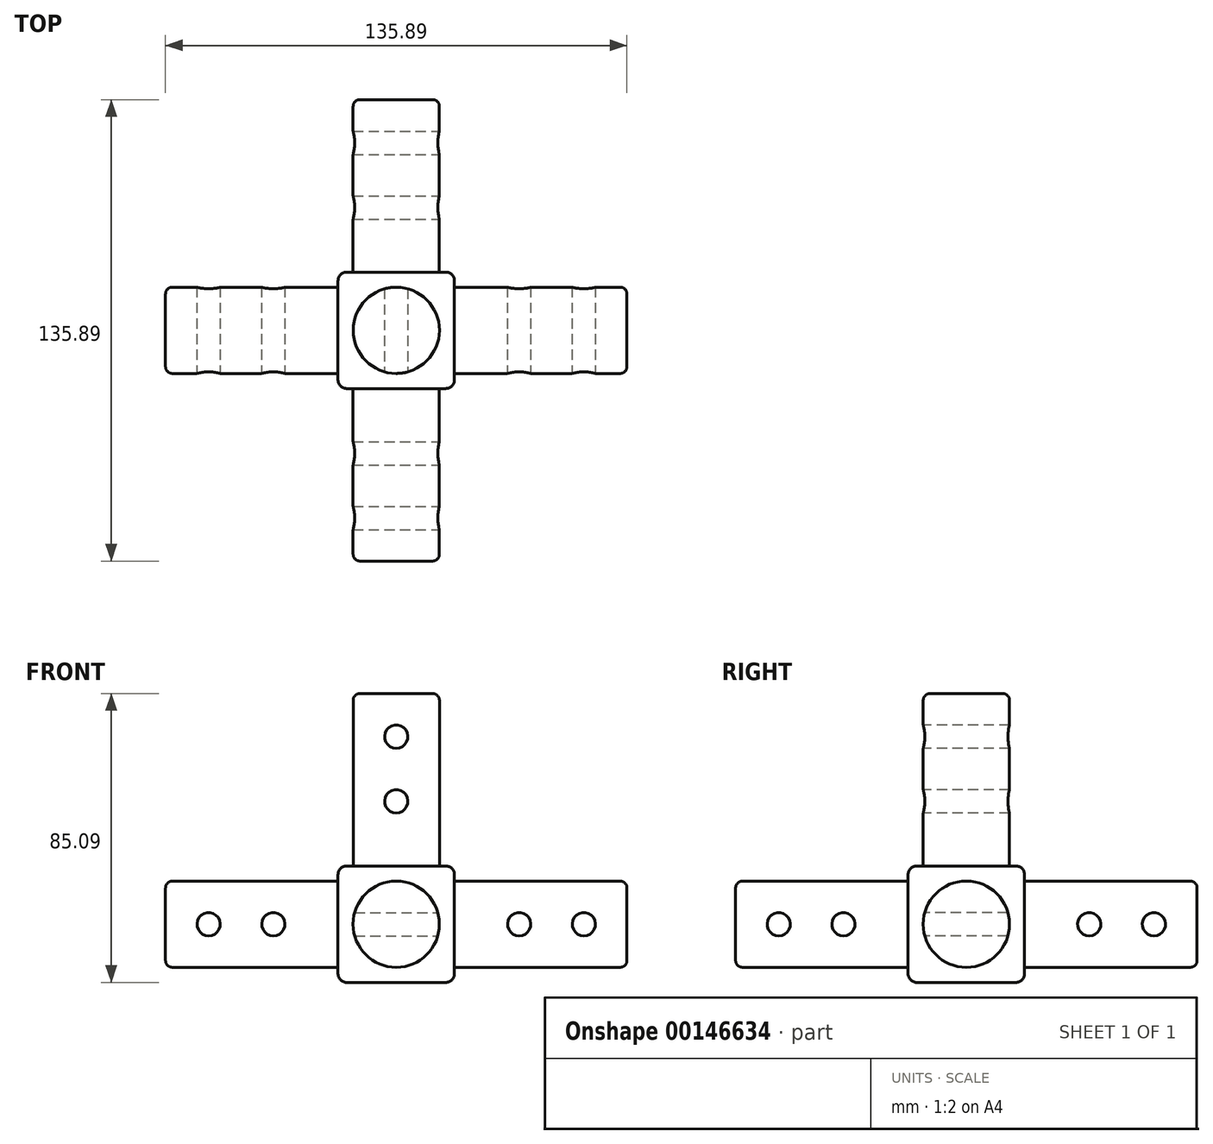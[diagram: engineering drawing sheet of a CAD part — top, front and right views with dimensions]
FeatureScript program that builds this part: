
annotation { "Feature Type Name" : "Feature", "Feature Type Description" : "" }
export const myFeature = defineFeature(function(context is Context, id is Id, definition is map)
    precondition{}
    {
        {
            var Q0;
            Q0=qCreatedBy(makeId("Top.planeOp"),FACE);
            var sketch = newSketch(context, id + "F0", { "sketchPlane" : qUnion([Q0])});
            skLineSegment(sketch, "E0.bottom", {"start": v(-13.47, 23.7) * mm, "end": v(20.82, 23.7) * mm});
            skLineSegment(sketch, "E0.top", {"start": v(-13.47, -10.58) * mm, "end": v(20.82, -10.58) * mm});
            skLineSegment(sketch, "E0.left", {"start": v(-13.47, 23.7) * mm, "end": v(-13.47, -10.58) * mm});
            skLineSegment(sketch, "E0.right", {"start": v(20.82, 23.7) * mm, "end": v(20.82, -10.58) * mm});
            skSolve(sketch);
        }
        {
            var Q0;
            Q0=qSketchRegion(id+"F0",true);
            extrude(context, id + "F1", {"entities" : qUnion([Q0]), "depth" : 34.3 * mm});
        }
        {
            var Q0;
            Q0=makeQuery(id+"F1.opExtrude","CAP_FACE",FACE,{"disambiguationData":[OSD([sQuery(id+"F0.wireOp",EDGE,"E0.bottom"),sQuery(id+"F0.wireOp",EDGE,"E0.top"),sQuery(id+"F0.wireOp",EDGE,"E0.left"),sQuery(id+"F0.wireOp",EDGE,"E0.right")])],"isStart":false});
            var sketch = newSketch(context, id + "F2", { "sketchPlane" : qUnion([Q0])});
            skCircle(sketch, "E1", {"center": v(3.68, 6.56) * mm, "radius": 12.7 * mm});
            skLineSegment(sketch, "E2", {"start": v(3.67, 23.7) * mm, "end": v(3.67, -12.79) * mm, "construction": true});
            skLineSegment(sketch, "E3", {"start": v(20.82, 6.56) * mm, "end": v(-13.47, 6.56) * mm, "construction": true});
            skSolve(sketch);
        }
        {
            var Q0;
            Q0=qSketchRegion(id+"F2",true);
            extrude(context, id + "F3", {"entities" : qUnion([Q0]), "operationType" : NewBodyOperationType.ADD, "depth" : 50.8 * mm});
        }
        {
            var Q0;
            Q0=makeQuery(id+"F1.opExtrude","SWEPT_FACE",FACE,{"disambiguationData":[OSD([sQuery(id+"F0.wireOp",EDGE,"E0.left")])]});
            var sketch = newSketch(context, id + "F4", { "sketchPlane" : qUnion([Q0])});
            skLineSegment(sketch, "E4", {"start": v(-23.7, 17.15) * mm, "end": v(13.45, 17.15) * mm, "construction": true});
            skLineSegment(sketch, "E5", {"start": v(-6.56, 0) * mm, "end": v(-6.56, 34.3) * mm, "construction": true});
            skCircle(sketch, "E6", {"center": v(-6.56, 17.15) * mm, "radius": 12.7 * mm});
            skSolve(sketch);
        }
        {
            var Q0;
            Q0=qSketchRegion(id+"F4",true);
            extrude(context, id + "F5", {"entities" : qUnion([Q0]), "operationType" : NewBodyOperationType.ADD, "depth" : 50.8 * mm});
        }
        {
            var Q0;
            Q0=makeQuery(id+"F1.opExtrude","SWEPT_FACE",FACE,{"disambiguationData":[OSD([sQuery(id+"F0.wireOp",EDGE,"E0.top")])]});
            var sketch = newSketch(context, id + "F6", { "sketchPlane" : qUnion([Q0])});
            skLineSegment(sketch, "E7", {"start": v(-13.47, 17.15) * mm, "end": v(24.43, 17.15) * mm, "construction": true});
            skLineSegment(sketch, "E8", {"start": v(3.67, 0) * mm, "end": v(3.67, 34.3) * mm, "construction": true});
            skCircle(sketch, "E9", {"center": v(3.67, 17.15) * mm, "radius": 12.7 * mm});
            skSolve(sketch);
        }
        {
            var Q0;
            Q0=qSketchRegion(id+"F6",true);
            extrude(context, id + "F7", {"entities" : qUnion([Q0]), "operationType" : NewBodyOperationType.ADD, "depth" : 50.8 * mm});
        }
        {
            var Q0;
            Q0=qCreatedBy(makeId("Front.planeOp"),FACE);
            var sketch = newSketch(context, id + "F8", { "sketchPlane" : qUnion([Q0])});
            skCircle(sketch, "E10", {"center": v(3.67, 53.34) * mm, "radius": 3.43 * mm});
            skCircle(sketch, "E11", {"center": v(3.67, 72.4) * mm, "radius": 3.43 * mm});
            skSolve(sketch);
        }
        {
            var Q0;
            Q0=qSketchRegion(id+"F8",true);
            extrude(context, id + "F9", {"entities" : qUnion([Q0]), "operationType" : NewBodyOperationType.REMOVE, "endBound" : BoundingType.SYMMETRIC, "oppositeDirection" : true, "depth" : 50.8 * mm});
        }
        {
            var Q0;
            Q0=qCreatedBy(makeId("Right.planeOp"),FACE);
            var sketch = newSketch(context, id + "F10", { "sketchPlane" : qUnion([Q0])});
            skCircle(sketch, "E12", {"center": v(-29.63, 17.15) * mm, "radius": 3.43 * mm});
            skCircle(sketch, "E13", {"center": v(-48.68, 17.15) * mm, "radius": 3.43 * mm});
            skSolve(sketch);
        }
        {
            var Q0;
            Q0=qSketchRegion(id+"F10",true);
            extrude(context, id + "F11", {"entities" : qUnion([Q0]), "operationType" : NewBodyOperationType.REMOVE, "endBound" : BoundingType.SYMMETRIC, "oppositeDirection" : true, "depth" : 50.8 * mm});
        }
        {
            var Q0;
            Q0=qCreatedBy(makeId("Front.planeOp"),FACE);
            var sketch = newSketch(context, id + "F12", { "sketchPlane" : qUnion([Q0])});
            skCircle(sketch, "E14", {"center": v(-51.57, 17.15) * mm, "radius": 3.43 * mm});
            skCircle(sketch, "E15", {"center": v(-32.52, 17.15) * mm, "radius": 3.43 * mm});
            skSolve(sketch);
        }
        {
            var Q0;
            Q0=qSketchRegion(id+"F12",true);
            extrude(context, id + "F13", {"entities" : qUnion([Q0]), "operationType" : NewBodyOperationType.REMOVE, "endBound" : BoundingType.SYMMETRIC, "oppositeDirection" : true, "depth" : 50.8 * mm});
        }
        {
            var Q0;
            Q0=makeQuery(id+"F1.opExtrude","SWEPT_EDGE",EDGE,{"disambiguationData":[OSD([sQuery(id+"F0.wireOp",EDGE,"E0.bottom"),sQuery(id+"F0.wireOp",EDGE,"E0.right")])]});
            var Q1;
            Q1=makeQuery(id+"F1.opExtrude","CAP_EDGE",EDGE,{"disambiguationData":[OSD([sQuery(id+"F0.wireOp",EDGE,"E0.right")])],"isStart":false});
            var Q2;
            Q2=makeQuery(id+"F1.opExtrude","SWEPT_EDGE",EDGE,{"disambiguationData":[OSD([sQuery(id+"F0.wireOp",EDGE,"E0.top"),sQuery(id+"F0.wireOp",EDGE,"E0.right")])]});
            var Q3;
            Q3=makeQuery(id+"F1.opExtrude","CAP_EDGE",EDGE,{"disambiguationData":[OSD([sQuery(id+"F0.wireOp",EDGE,"E0.right")])],"isStart":true});
            var Q4;
            Q4=makeQuery(id+"F1.opExtrude","CAP_EDGE",EDGE,{"disambiguationData":[OSD([sQuery(id+"F0.wireOp",EDGE,"E0.bottom")])],"isStart":true});
            var Q5;
            Q5=makeQuery(id+"F1.opExtrude","CAP_EDGE",EDGE,{"disambiguationData":[OSD([sQuery(id+"F0.wireOp",EDGE,"E0.bottom")])],"isStart":false});
            var Q6;
            Q6=makeQuery(id+"F1.opExtrude","SWEPT_EDGE",EDGE,{"disambiguationData":[OSD([sQuery(id+"F0.wireOp",EDGE,"E0.bottom"),sQuery(id+"F0.wireOp",EDGE,"E0.left")])]});
            var Q7;
            Q7=makeQuery(id+"F1.opExtrude","CAP_EDGE",EDGE,{"disambiguationData":[OSD([sQuery(id+"F0.wireOp",EDGE,"E0.left")])],"isStart":true});
            var Q8;
            Q8=makeQuery(id+"F1.opExtrude","CAP_EDGE",EDGE,{"disambiguationData":[OSD([sQuery(id+"F0.wireOp",EDGE,"E0.top")])],"isStart":true});
            var Q9;
            Q9=makeQuery(id+"F1.opExtrude","CAP_EDGE",EDGE,{"disambiguationData":[OSD([sQuery(id+"F0.wireOp",EDGE,"E0.left")])],"isStart":false});
            var Q10;
            Q10=makeQuery(id+"F1.opExtrude","SWEPT_EDGE",EDGE,{"disambiguationData":[OSD([sQuery(id+"F0.wireOp",EDGE,"E0.top"),sQuery(id+"F0.wireOp",EDGE,"E0.left")])]});
            var Q11;
            Q11=makeQuery(id+"F1.opExtrude","CAP_EDGE",EDGE,{"disambiguationData":[OSD([sQuery(id+"F0.wireOp",EDGE,"E0.top")])],"isStart":false});
            fillet(context, id + "F14", {"entities" : qUnion([Q0, Q1, Q2, Q3, Q4, Q5, Q6, Q7, Q8, Q9, Q10, Q11]), "radius" : 2.54 * mm, "tangentPropagation" : true, "allowEdgeOverflow" : false});
        }
        {
            var Q0;
            Q0=makeQuery(id+"F1.opExtrude","SWEPT_FACE",FACE,{"disambiguationData":[OSD([sQuery(id+"F0.wireOp",EDGE,"E0.bottom")])]});
            var sketch = newSketch(context, id + "F15", { "sketchPlane" : qUnion([Q0])});
            skLineSegment(sketch, "E16", {"start": v(-18.28, 17.15) * mm, "end": v(4.82, 17.15) * mm, "construction": true});
            skPoint(sketch, "E16.endSnap0", {"position": v(-18.28, 17.15) * mm});
            skLineSegment(sketch, "E17", {"start": v(-3.67, 31.75) * mm, "end": v(-3.67, 14.65) * mm, "construction": true});
            skCircle(sketch, "E18", {"center": v(-3.67, 17.15) * mm, "radius": 12.7 * mm});
            skSolve(sketch);
        }
        {
            var Q0;
            Q0=qSketchRegion(id+"F15",true);
            extrude(context, id + "F16", {"entities" : qUnion([Q0]), "operationType" : NewBodyOperationType.ADD, "depth" : 50.8 * mm});
        }
        {
            var Q0;
            Q0=qCreatedBy(makeId("Right.planeOp"),FACE);
            var sketch = newSketch(context, id + "F17", { "sketchPlane" : qUnion([Q0])});
            skCircle(sketch, "E19", {"center": v(42.76, 17.15) * mm, "radius": 3.43 * mm});
            skCircle(sketch, "E20", {"center": v(61.8, 17.15) * mm, "radius": 3.43 * mm});
            skSolve(sketch);
        }
        {
            var Q0;
            Q0=qSketchRegion(id+"F17",true);
            extrude(context, id + "F18", {"entities" : qUnion([Q0]), "operationType" : NewBodyOperationType.REMOVE, "endBound" : BoundingType.SYMMETRIC, "oppositeDirection" : true, "depth" : 50.8 * mm});
        }
        {
            var Q0;
            Q0=makeQuery(id+"F1.opExtrude","SWEPT_FACE",FACE,{"disambiguationData":[OSD([sQuery(id+"F0.wireOp",EDGE,"E0.right")])]});
            var sketch = newSketch(context, id + "F19", { "sketchPlane" : qUnion([Q0])});
            skCircle(sketch, "E21", {"center": v(6.56, 17.14) * mm, "radius": 12.7 * mm});
            skLineSegment(sketch, "E22", {"start": v(-8.04, 17.15) * mm, "end": v(28.63, 17.15) * mm, "construction": true});
            skLineSegment(sketch, "E23", {"start": v(6.56, 2.54) * mm, "end": v(6.56, 27.82) * mm, "construction": true});
            skSolve(sketch);
        }
        {
            var Q0;
            Q0 = qSketchRegion(id + "F19", true);
            extrude(context, id + "F20", {"entities" : qUnion([Q0]), "operationType" : NewBodyOperationType.ADD, "depth" : 50.8 * mm});
        }
        {
            var Q0;
            Q0=makeQuery(id+"F3.opExtrude","CAP_EDGE",EDGE,{"disambiguationData":[OSD([sQuery(id+"F2.wireOp",EDGE,"E1")])],"isStart":false});
            var Q1;
            Q1=makeQuery(id+"F7.opExtrude","CAP_EDGE",EDGE,{"disambiguationData":[OSD([sQuery(id+"F6.wireOp",EDGE,"E9")])],"isStart":false});
            var Q2;
            Q2=makeQuery(id+"F5.opExtrude","CAP_EDGE",EDGE,{"disambiguationData":[OSD([sQuery(id+"F4.wireOp",EDGE,"E6")])],"isStart":false});
            var Q3;
            Q3=makeQuery(id+"F16.opExtrude","CAP_EDGE",EDGE,{"disambiguationData":[OSD([sQuery(id+"F15.wireOp",EDGE,"E18")])],"isStart":false});
            var Q4;
            Q4=makeQuery(id+"F20.opExtrude","CAP_EDGE",EDGE,{"disambiguationData":[OSD([sQuery(id+"F19.wireOp",EDGE,"E21")])],"isStart":false});
            fillet(context, id + "F21", {"entities" : qUnion([Q0, Q1, Q2, Q3, Q4]), "radius" : 2.03 * mm, "tangentPropagation" : true, "allowEdgeOverflow" : false});
        }
        {
            var Q0;
            Q0=qCreatedBy(makeId("Front.planeOp"),FACE);
            var sketch = newSketch(context, id + "F22", { "sketchPlane" : qUnion([Q0])});
            skCircle(sketch, "E24", {"center": v(58.92, 17.15) * mm, "radius": 3.43 * mm});
            skCircle(sketch, "E25", {"center": v(39.87, 17.15) * mm, "radius": 3.43 * mm});
            skSolve(sketch);
        }
        {
            var Q0;
            Q0 = qSketchRegion(id + "F22", true);
            extrude(context, id + "F23", {"entities" : qUnion([Q0]), "operationType" : NewBodyOperationType.REMOVE, "endBound" : BoundingType.SYMMETRIC, "oppositeDirection" : true, "depth" : 50.8 * mm});
        }
    });
